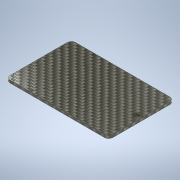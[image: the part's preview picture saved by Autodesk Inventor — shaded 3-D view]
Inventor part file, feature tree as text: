
AUTODESK INVENTOR PART (.ipt)
format: ipt  version: 2020 (Build 240168000, 168)  size: 137,216 bytes
history: native  units: in
note: dims shown in document units (in); Inventor stores cm internally (conversion verified against a paired STEP export)
features: extrude x2, sketch x1, fillet x1, direct_edit x1, move_body x1
ambient origin geometry x8: Origin, YZ Plane, XZ Plane, XY Plane, X Axis, Y Axis, Z Axis, Center Point
bodies: Solid1 (feature_tree)
feature tree (6):
  sketch  "Sketch1"  dims[d0=3.843in d1=2.446in d2=0.0787in d3=0.906in d4=0.0787in d5=0.1772in d6=0.1969in d7=0.1181in d8=0.0in d9=0.0394in d10=0.0in d11=0.1575in d12=0.0in d13=0.0in d14=-0.0197in]
  extrude  "Extrusion1"  Depth=2.446in
  extrude  "Extrusion2"  Depth=0.0787in
  fillet  "Fillet1"  Radius=0.906in
  direct_edit  "Direct Edit1"
  move_body  "Move1"
